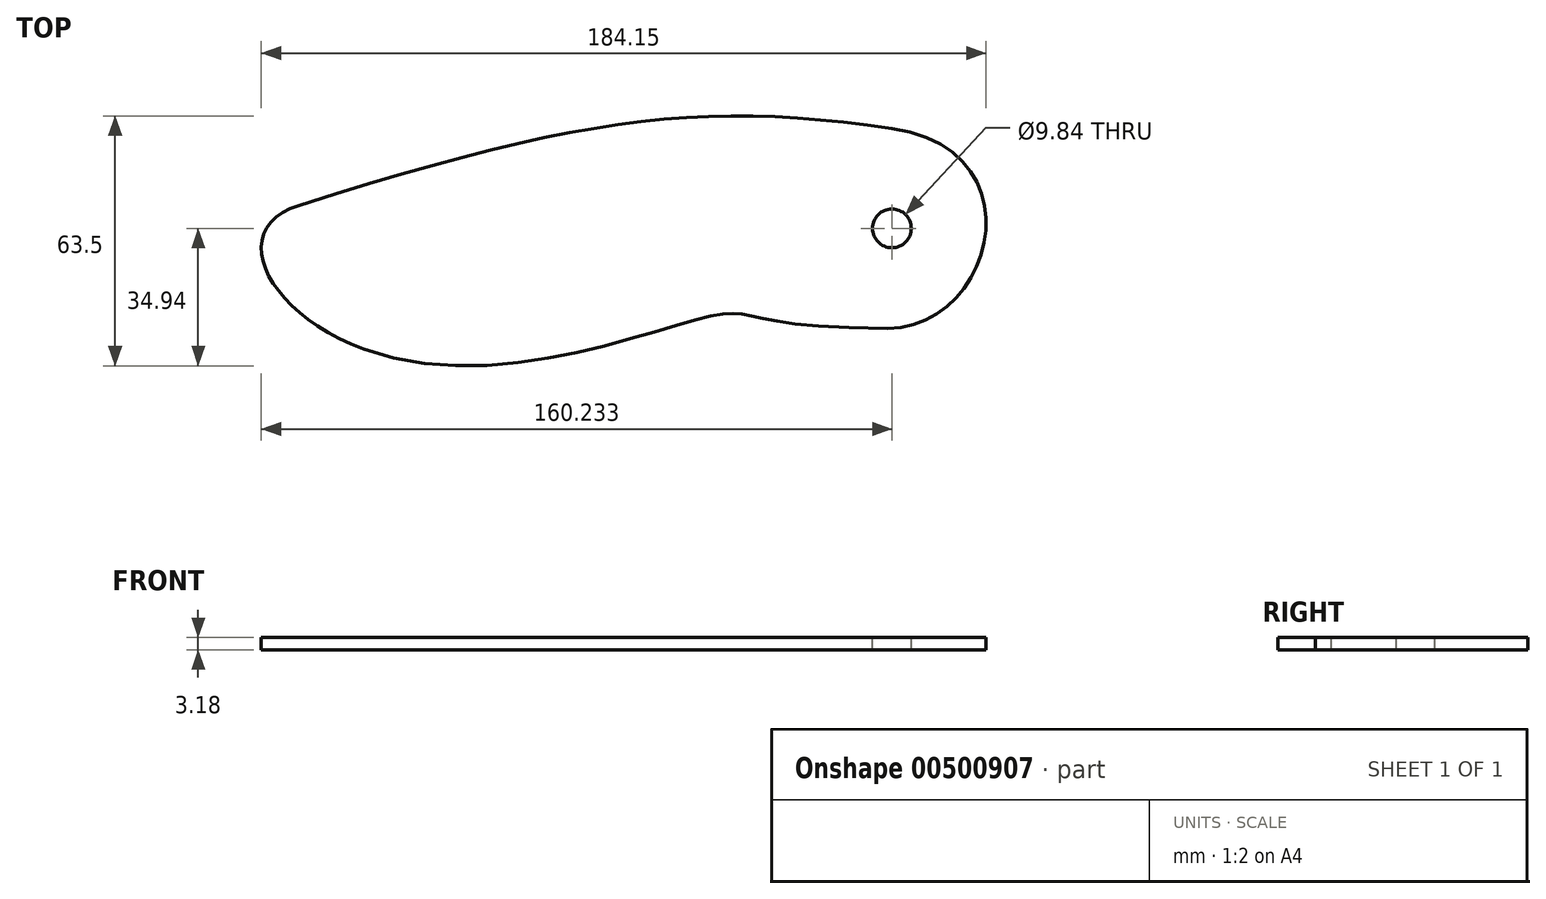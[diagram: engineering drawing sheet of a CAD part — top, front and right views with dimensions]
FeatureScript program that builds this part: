
annotation { "Feature Type Name" : "Feature", "Feature Type Description" : "" }
export const myFeature = defineFeature(function(context is Context, id is Id, definition is map)
    precondition{}
    {
        {
            var Q0;
            Q0=qCreatedBy(makeId("Top.planeOp"),FACE);
            var sketch = newSketch(context, id + "F0", { "sketchPlane" : qUnion([Q0])});
            skFitSpline(sketch, "E0", {"points": [v(-102.95, -0.43) * mm, v(0, 0) * mm, v(44.75, -3.18) * mm], "startDerivative": vector(171.63, -128.95) * mm, "endDerivative": vector(271.87, 0) * mm});
            skFitSpline(sketch, "E1", {"points": [v(44.75, -3.18) * mm, v(45.93, 47.63) * mm], "startDerivative": vector(81.05, 0) * mm, "endDerivative": vector(-113.08, 16.5) * mm});
            skFitSpline(sketch, "E2", {"points": [v(-104.7, 28.09) * mm, v(45.93, 47.63) * mm], "startDerivative": vector(214.59, 67.9) * mm, "endDerivative": vector(145.24, -21.18) * mm});
            skFitSpline(sketch, "E3", {"points": [v(-88.24, -8.42) * mm, v(-104.7, 28.09) * mm], "startDerivative": vector(-75.23, 27.84) * mm, "endDerivative": vector(55.78, 17.65) * mm});
            skLineSegment(sketch, "E4", {"start": v(-114.3, 4.24) * mm, "end": v(-114.3, 71.3) * mm, "construction": true});
            skLineSegment(sketch, "E5", {"start": v(69.85, 74.79) * mm, "end": v(69.85, -33.43) * mm, "construction": true});
            skLineSegment(sketch, "E6", {"start": v(6.74, 50.8) * mm, "end": v(-101.88, 50.8) * mm, "construction": true});
            skLineSegment(sketch, "E7", {"start": v(44.75, -3.18) * mm, "end": v(221.6, -3.18) * mm, "construction": true});
            skLineSegment(sketch, "E8", {"start": v(-62.32, -12.7) * mm, "end": v(-195.5, -12.7) * mm, "construction": true});
            skSolve(sketch);
        }
        {
            var Q0;
            Q0=makeQuery(id+"F0.imprint","IMPRINT",FACE,{"disambiguationData":[TD([[makeQuery(id+"F0.imprint","IMPRINT",EDGE,{"derivedFrom":sQuery(id+"F0.wireOp",EDGE,"E0")}),1.0]])]});
            extrude(context, id + "F1", {"entities" : qUnion([Q0]), "depth" : 3.17 * mm});
        }
        {
            var Q0;
            Q0=makeQuery(id+"F1.opExtrude","CAP_FACE",FACE,{"disambiguationData":[OSD([sQuery(id+"F0.wireOp",EDGE,"E0"),sQuery(id+"F0.wireOp",EDGE,"E1"),sQuery(id+"F0.wireOp",EDGE,"E2"),sQuery(id+"F0.wireOp",EDGE,"E3")])],"isStart":false});
            var sketch = newSketch(context, id + "F2", { "sketchPlane" : qUnion([Q0])});
            skCircle(sketch, "E9", {"center": v(45.93, 22.24) * mm, "radius": 4.92 * mm});
            skFitSpline(sketch, "E10.0", {"points": [v(44.75, -3.18) * mm, v(71.77, -3.18) * mm, v(83.63, 42.13) * mm, v(45.93, 47.63) * mm]});
            skLineSegment(sketch, "E11", {"start": v(45.93, 47.63) * mm, "end": v(45.93, -3.15) * mm, "construction": true});
            skSolve(sketch);
        }
        {
            var Q0;
            Q0=makeQuery(id+"F2.imprint","IMPRINT",FACE,{"disambiguationData":[TD([[makeQuery(id+"F2.imprint","IMPRINT",EDGE,{"derivedFrom":sQuery(id+"F2.wireOp",EDGE,"E9")}),1.0]])]});
            extrude(context, id + "F3", {"entities" : qUnion([Q0]), "operationType" : NewBodyOperationType.REMOVE, "oppositeDirection" : true, "depth" : 25.4 * mm});
        }
    });
